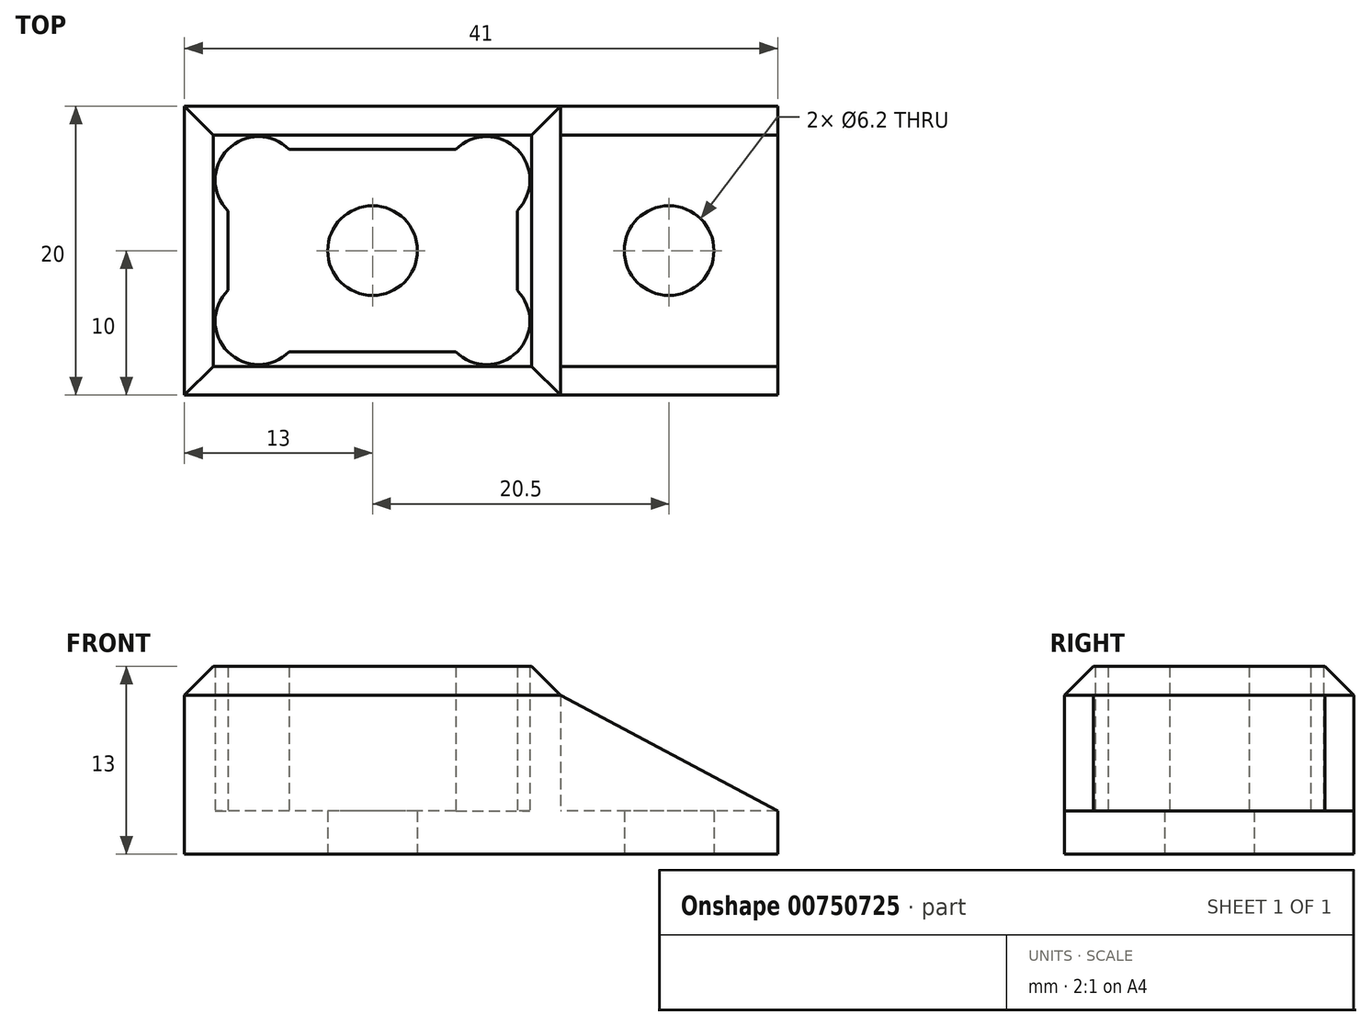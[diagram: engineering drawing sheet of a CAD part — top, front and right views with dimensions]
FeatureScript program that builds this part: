
annotation { "Feature Type Name" : "Feature", "Feature Type Description" : "" }
export const myFeature = defineFeature(function(context is Context, id is Id, definition is map)
    precondition{}
    {
        {
            var Q0;
            Q0=qCreatedBy(makeId("Top.planeOp"),FACE);
            var sketch = newSketch(context, id + "F0", { "sketchPlane" : qUnion([Q0])});
            skLineSegment(sketch, "E0.bottom", {"start": v(10, -7) * mm, "end": v(-10, -7) * mm, "construction": true});
            skLineSegment(sketch, "E0.top", {"start": v(10, 7) * mm, "end": v(-10, 7) * mm, "construction": true});
            skLineSegment(sketch, "E0.left", {"start": v(10, -7) * mm, "end": v(10, 7) * mm, "construction": true});
            skLineSegment(sketch, "E0.right", {"start": v(-10, -7) * mm, "end": v(-10, 7) * mm, "construction": true});
            skPoint(sketch, "E0.middle", {"position": v(0, 0) * mm});
            skLineSegment(sketch, "E1.0", {"start": v(13, -10) * mm, "end": v(13, 10) * mm, "construction": true});
            skLineSegment(sketch, "E1.1", {"start": v(13, -10) * mm, "end": v(-13, -10) * mm});
            skLineSegment(sketch, "E1.2", {"start": v(-13, -10) * mm, "end": v(-13, 10) * mm});
            skLineSegment(sketch, "E1.3", {"start": v(13, 10) * mm, "end": v(-13, 10) * mm});
            skLineSegment(sketch, "E2", {"start": v(13, -10) * mm, "end": v(28, -10) * mm});
            skLineSegment(sketch, "E3", {"start": v(28, -10) * mm, "end": v(28, 10) * mm});
            skLineSegment(sketch, "E4", {"start": v(28, 10) * mm, "end": v(13, 10) * mm});
            skLineSegment(sketch, "E5", {"start": v(20.5, -10) * mm, "end": v(20.5, 10) * mm, "construction": true});
            skCircle(sketch, "E6", {"center": v(20.5, 0) * mm, "radius": 3.1 * mm});
            skCircle(sketch, "E7", {"center": v(20.5, 0) * mm, "radius": 7.5 * mm, "construction": true});
            skCircle(sketch, "E8", {"center": v(0, 0) * mm, "radius": 3.1 * mm});
            skSolve(sketch);
        }
        {
            var Q0;
            Q0=qSketchRegion(id+"F0",true);
            extrude(context, id + "F1", {"entities" : qUnion([Q0]), "depth" : 3 * mm, "offsetDistance" : 25 * mm});
        }
        {
            var Q0;
            Q0=makeQuery(id+"F1.opExtrude","CAP_FACE",FACE,{"disambiguationData":[OSD([sQuery(id+"F0.wireOp",EDGE,"E1.1"),sQuery(id+"F0.wireOp",EDGE,"E1.2"),sQuery(id+"F0.wireOp",EDGE,"E1.3"),sQuery(id+"F0.wireOp",EDGE,"E2"),sQuery(id+"F0.wireOp",EDGE,"E3"),sQuery(id+"F0.wireOp",EDGE,"E4"),sQuery(id+"F0.wireOp",EDGE,"E6")])],"isStart":false});
            var sketch = newSketch(context, id + "F2", { "sketchPlane" : qUnion([Q0])});
            skLineSegment(sketch, "E9.0", {"start": v(-10, -7) * mm, "end": v(-10, -2.76) * mm, "construction": true});
            skLineSegment(sketch, "E9.1", {"start": v(10, 7) * mm, "end": v(5.76, 7) * mm, "construction": true});
            skLineSegment(sketch, "E9.2", {"start": v(10, -7) * mm, "end": v(10, -2.76) * mm, "construction": true});
            skLineSegment(sketch, "E9.3", {"start": v(10, -7) * mm, "end": v(5.76, -7) * mm, "construction": true});
            skLineSegment(sketch, "E10.0", {"start": v(13, -10) * mm, "end": v(-13, -10) * mm});
            skLineSegment(sketch, "E10.1", {"start": v(-13, -10) * mm, "end": v(-13, 10) * mm});
            skLineSegment(sketch, "E10.2", {"start": v(13, 10) * mm, "end": v(-13, 10) * mm});
            skLineSegment(sketch, "E11.0", {"start": v(13, -10) * mm, "end": v(13, 10) * mm});
            skArc(sketch, "E12", {"start": v(-5.76, 7) * mm, "mid": v(-10, 7) * mm, "end": v(-10, 2.76) * mm});
            skArc(sketch, "E13", {"start": v(10, 2.76) * mm, "mid": v(10, 7) * mm, "end": v(5.76, 7) * mm});
            skArc(sketch, "E14", {"start": v(5.76, -7) * mm, "mid": v(10, -7) * mm, "end": v(10, -2.76) * mm});
            skArc(sketch, "E15", {"start": v(-10, -2.76) * mm, "mid": v(-10, -7) * mm, "end": v(-5.76, -7) * mm});
            skLineSegment(sketch, "E16", {"start": v(-10, 7) * mm, "end": v(-7.88, 4.88) * mm, "construction": true});
            skLineSegment(sketch, "E17", {"start": v(-5.76, 7) * mm, "end": v(-10, 7) * mm, "construction": true});
            skLineSegment(sketch, "E18", {"start": v(-10, 2.76) * mm, "end": v(-10, 7) * mm, "construction": true});
            skLineSegment(sketch, "E19", {"start": v(5.76, 7) * mm, "end": v(-5.76, 7) * mm});
            skLineSegment(sketch, "E20", {"start": v(10, 2.76) * mm, "end": v(10, 7) * mm, "construction": true});
            skLineSegment(sketch, "E21", {"start": v(10, -2.76) * mm, "end": v(10, 2.76) * mm});
            skLineSegment(sketch, "E22", {"start": v(5.76, -7) * mm, "end": v(-5.76, -7) * mm});
            skLineSegment(sketch, "E23", {"start": v(-5.76, -7) * mm, "end": v(-10, -7) * mm, "construction": true});
            skLineSegment(sketch, "E24", {"start": v(-10, -2.76) * mm, "end": v(-10, 2.76) * mm});
            skSolve(sketch);
        }
        {
            var Q0;
            Q0 = qSketchRegion(id + "F2", true);
            extrude(context, id + "F3", {"entities" : qUnion([Q0]), "operationType" : NewBodyOperationType.ADD, "depth" : 10 * mm, "offsetDistance" : 25 * mm});
        }
        {
            var Q0;
            Q0=makeQuery(id+"F3.opExtrude","CAP_EDGE",EDGE,{"disambiguationData":[OSD([sQuery(id+"F2.wireOp",EDGE,"E10.0")])],"isStart":false});
            var Q1;
            Q1=makeQuery(id+"F3.opExtrude","CAP_EDGE",EDGE,{"disambiguationData":[OSD([sQuery(id+"F2.wireOp",EDGE,"E11.0")])],"isStart":false});
            var Q2;
            Q2=makeQuery(id+"F3.opExtrude","CAP_EDGE",EDGE,{"disambiguationData":[OSD([sQuery(id+"F2.wireOp",EDGE,"E10.2")])],"isStart":false});
            var Q3;
            Q3=makeQuery(id+"F3.opExtrude","CAP_EDGE",EDGE,{"disambiguationData":[OSD([sQuery(id+"F2.wireOp",EDGE,"E10.1")])],"isStart":false});
            chamfer(context, id + "F4", {"entities" : qUnion([Q0, Q1, Q2, Q3]), "width" : 2 * mm, "tangentPropagation" : true});
        }
        {
            var Q0;
            Q0=makeQuery(id+"F3.boolean.opBoolean","MERGE",FACE,{"derivedFrom":[makeQuery(id+"F1.opExtrude","SWEPT_FACE",FACE,{"disambiguationData":[OSD([sQuery(id+"F0.wireOp",EDGE,"E1.1"),sQuery(id+"F0.wireOp",EDGE,"E2")])]}),makeQuery(id+"F3.opExtrude","SWEPT_FACE",FACE,{"disambiguationData":[OSD([sQuery(id+"F2.wireOp",EDGE,"E10.0")])]})]});
            var sketch = newSketch(context, id + "F5", { "sketchPlane" : qUnion([Q0])});
            skLineSegment(sketch, "E25", {"start": v(13, 11) * mm, "end": v(28, 3) * mm});
            skLineSegment(sketch, "E26.0", {"start": v(13, 11) * mm, "end": v(13, 3) * mm});
            skLineSegment(sketch, "E26.1", {"start": v(28, 3) * mm, "end": v(13, 3) * mm});
            skSolve(sketch);
        }
        {
            var Q0;
            Q0 = qSketchRegion(id + "F5", true);
            extrude(context, id + "F6", {"entities" : qUnion([Q0]), "operationType" : NewBodyOperationType.ADD, "oppositeDirection" : true, "depth" : 2 * mm, "offsetDistance" : 25 * mm});
        }
        {
            var Q0;
            Q0=makeQuery(id+"F3.boolean.opBoolean","MERGE",FACE,{"derivedFrom":[makeQuery(id+"F1.opExtrude","SWEPT_FACE",FACE,{"disambiguationData":[OSD([sQuery(id+"F0.wireOp",EDGE,"E1.3"),sQuery(id+"F0.wireOp",EDGE,"E4")])]}),makeQuery(id+"F3.opExtrude","SWEPT_FACE",FACE,{"disambiguationData":[OSD([sQuery(id+"F2.wireOp",EDGE,"E10.2")])]})]});
            var sketch = newSketch(context, id + "F7", { "sketchPlane" : qUnion([Q0])});
            skLineSegment(sketch, "E27", {"start": v(-13, 11) * mm, "end": v(-28, 3) * mm});
            skLineSegment(sketch, "E28.0", {"start": v(-28, 3) * mm, "end": v(-13, 3) * mm});
            skLineSegment(sketch, "E28.1", {"start": v(-13, 11) * mm, "end": v(-13, 3) * mm});
            skSolve(sketch);
        }
        {
            var Q0;
            Q0 = qSketchRegion(id + "F7", true);
            extrude(context, id + "F8", {"entities" : qUnion([Q0]), "operationType" : NewBodyOperationType.ADD, "oppositeDirection" : true, "depth" : 2 * mm, "offsetDistance" : 25 * mm});
        }
    });
